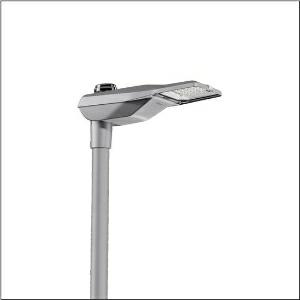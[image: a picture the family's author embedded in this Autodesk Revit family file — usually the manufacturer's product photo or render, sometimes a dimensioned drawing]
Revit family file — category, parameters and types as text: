
# Revit family: streetlight_sl_21_micro___p0_8a_5xe5u27n08db_ddcc
name_source: partatom
category: Lighting Fixtures
units: mm (PartAtom-declared; Revit-internal decimal feet)

## family parameters
Cut with Voids When Loaded = No
Host = Face
Light Source = No
Part Type = Normal
Room Calculation Point = No
Round Connector Dimension = Use Diameter
Shared = No

## types (1)
- --- (1 x LED, 4180 lm, 39.1 W, 2200K)
    Apparent Load = 39 VA
    CIE Flux Codes = 33 69 96 100 100
    Color Rendering = 70
    Color Temperature = 2200K
    Default Elevation = 1800 mm
    Description = Streetlight SL 21 micro, mast luminaire, primary light control with lens, of PMMA, primary optical cover: cover, of toughened safety glass, transparent, light distribution: P0.8a, light emission: direct distribution, primary light characteristic: asymmetric, installation type: post-top, LED, 3G 1.5mm², High Power LED, rated luminous flux: 4.180lm, luminous efficacy: 107lm/W, light colour: 722, colour temperature: 2200K, control gear: NEMA (7pin), control: flexible luminous flux parameterisation, time-dependent luminous flux control, constant luminous flux control, pre-setting: linear dimming characteristic, overheat protection, mains connection: 230..240V, AC, 50/60Hz, connection cable pre-assembled, cable length: 6,5m, wiring characteristics: H07RN-F, start of lifetime: 39W, end of service life: 41W, reduction: 18W, luminaire housing, of diecast aluminium (EN AC-44300), powder-coated, Siteco® metallic grey (DB 702S), corrosivity category C5 mid according to DIN EN ISO 12944, multi-level sealing system, sealing non-destructively replaceable, inclination adjustable: 0°, 5°, 10°, 15°, length: 528mm, width: 235mm, height: 110mm, spigot size: 76/60mm (post-top), mounting height: 4..8m, protection rating (complete): IP66, insulation class (complete): insulation class I (protective earthing), certification: CE, ENEC, ENEC+, VDE, impact resistance: IK10, permissible operating ambient temperature for outdoor applications: -40..+50°C, standard-compliant lighting for roads and squares, packaging unit: 1 piece

Light Distribution: P0.8a
    Height = 110 mm
    Lamp = 1 x LED
    Lamp Light Flux = 4180 lm
    Lamp Power = 39.1 W
    Lamp count = 1
    Length = 528 mm
    Luminous efficacy = 107 lm/W
    Manufacturer = Siteco
    ModVariant = No
    Model = 5XE5U27N08DB
    Number of Poles = 1
    OnlyDefault = Yes
    Power Factor = 1
    Product Name = Streetlight SL 21 micro | P0.8a
    Product group = mast luminaire | pylon top
    ProductGroupID = 6100
    Protection Class = Protection class I
    Protection Degree = IP 66
    RLX_Detail_Level = 1
    RLX_Emergency_Light_Flux = 0 lm
    RLX_Emergency_Type = 0
    RLX_Emergency_Type_DB = No
    RlxData = <blob elided: 98861 chars, md5=f3a3dc48>
    Socket = socket
    Standby Power = 0 W
    System Light Flux = 4180 lm
    System Power = 39 W
    Type Comments = factory setting: luminous flux: 100 % | dim-lin: 254 | 765 mA
    Type Image = l_1294375.jpg
    URL = http://relux.com
    VarID = @adj_073838
    Voltage = 0 V
    Weight = 0.00 kg
    Width = 235 mm

## geometry (parser evidence)
native form markers: Blend x4, Sweep x9
no freeform markers — native parametric forms only
